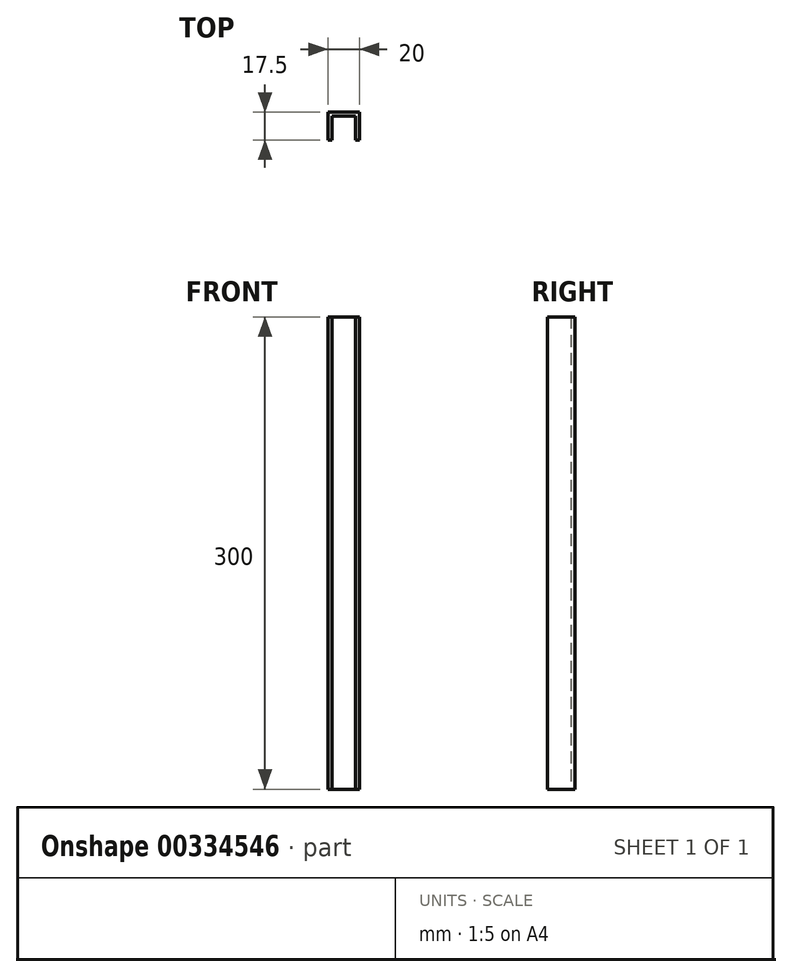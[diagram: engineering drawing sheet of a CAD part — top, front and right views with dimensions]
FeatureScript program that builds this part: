
annotation { "Feature Type Name" : "Feature", "Feature Type Description" : "" }
export const myFeature = defineFeature(function(context is Context, id is Id, definition is map)
    precondition{}
    {
        {
            var Q0;
            Q0=qCreatedBy(makeId("Top.planeOp"),FACE);
            var sketch = newSketch(context, id + "F0", { "sketchPlane" : qUnion([Q0])});
            skLineSegment(sketch, "E0.bottom", {"start": v(10, -10) * mm, "end": v(-10, -10) * mm});
            skLineSegment(sketch, "E0.top", {"start": v(10, 10) * mm, "end": v(-10, 10) * mm});
            skLineSegment(sketch, "E0.left", {"start": v(10, -10) * mm, "end": v(10, 10) * mm});
            skLineSegment(sketch, "E0.right", {"start": v(-10, -10) * mm, "end": v(-10, 10) * mm});
            skPoint(sketch, "E0.middle", {"position": v(0, 0) * mm});
            skLineSegment(sketch, "E1.bottom", {"start": v(7.5, -7.5) * mm, "end": v(-7.5, -7.5) * mm});
            skLineSegment(sketch, "E1.top", {"start": v(7.5, 7.5) * mm, "end": v(-7.5, 7.5) * mm});
            skLineSegment(sketch, "E1.left", {"start": v(7.5, -7.5) * mm, "end": v(7.5, 7.5) * mm});
            skLineSegment(sketch, "E1.right", {"start": v(-7.5, -7.5) * mm, "end": v(-7.5, 7.5) * mm});
            skLineSegment(sketch, "E2.bottom", {"start": v(-10, -7.5) * mm, "end": v(10, -7.5) * mm});
            skLineSegment(sketch, "E2.top", {"start": v(-10, -10) * mm, "end": v(10, -10) * mm});
            skLineSegment(sketch, "E2.left", {"start": v(-10, -7.5) * mm, "end": v(-10, -10) * mm});
            skLineSegment(sketch, "E2.right", {"start": v(10, -7.5) * mm, "end": v(10, -10) * mm});
            skSolve(sketch);
        }
        {
            var Q0;
            Q0=makeQuery(id+"F0.imprint","IMPRINT",FACE,{"disambiguationData":[TD([[makeQuery(id+"F0.imprint","IMPRINT",EDGE,{"derivedFrom":sQuery(id+"F0.wireOp",EDGE,"E0.top")}),1.0]])]});
            extrude(context, id + "F1", {"entities" : qUnion([Q0]), "depth" : 300 * mm});
        }
    });
